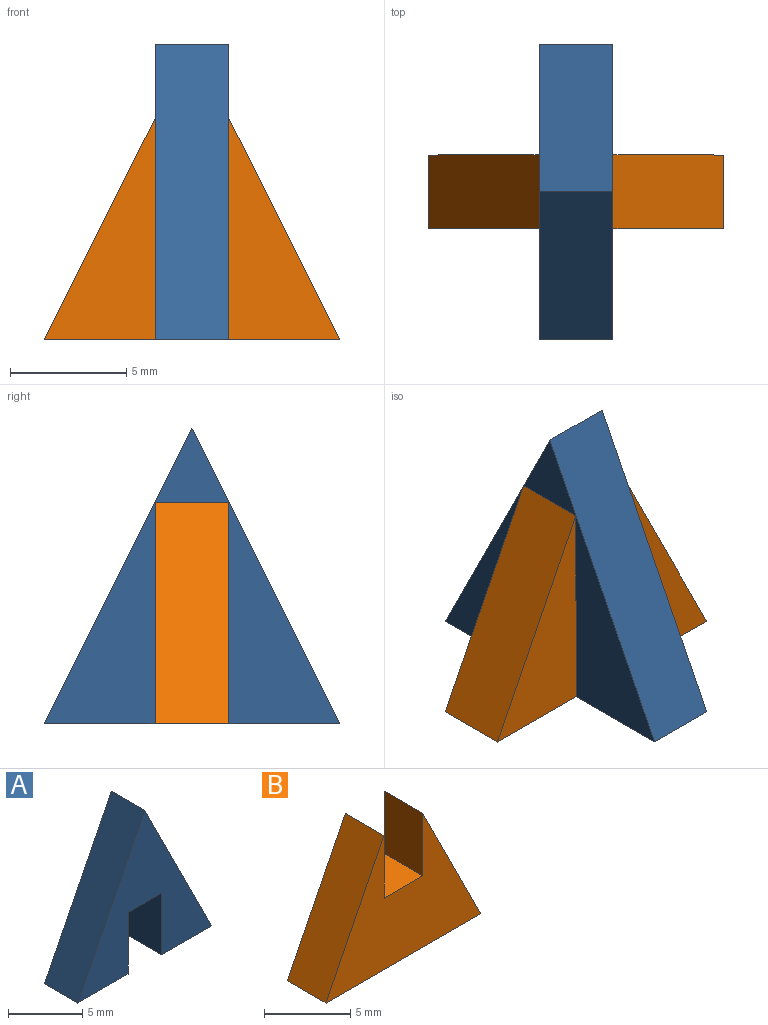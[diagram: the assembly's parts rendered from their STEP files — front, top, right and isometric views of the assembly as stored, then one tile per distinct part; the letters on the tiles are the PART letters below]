
ASSEMBLY  parts=2 mates=1
PART A: 9 faces, bbox 12.7x3.2x12.7 mm
  f0: plane 5.08x3.18mm, normal (-1,0,0), area 16.1mm2, adj f1,f6,f7,f8
  f1: plane 4.76x3.18mm, normal (0,0,-1), area 15.1mm2, adj f0,f2,f7,f8
  f2: plane 12.7x6.35mm, normal (0.89,0,0.45), area 45.1mm2, adj f1,f3,f7,f8
  f3: plane 12.7x6.35mm, normal (-0.89,0,0.45), area 45.1mm2, adj f2,f4,f7,f8
  f4: plane 4.76x3.18mm, normal (0,0,-1), area 15.1mm2, adj f3,f5,f7,f8
  f5: plane 5.08x3.18mm, normal (1,0,0), area 16.1mm2, adj f4,f6,f7,f8
  f6: plane 3.18x3.18mm, normal (0,0,-1), area 10.1mm2, adj f0,f5,f7,f8
  f7: plane 12.7x12.7mm, normal (0,-1,0), area 64.5mm2, adj f0,f1,f2,f3,f4,f5,f6
  f8: plane 12.7x12.7mm, normal (0,1,0), area 64.5mm2, adj f0,f1,f2,f3,f4,f5,f6
PART B: 8 faces, bbox 12.7x3.2x9.5 mm
  f0: plane 12.7x3.18mm, normal (0,0,-1), area 40.3mm2, adj f1,f5,f6,f7
  f1: plane 9.53x4.76mm, normal (0.89,0,0.45), area 33.8mm2, adj f0,f2,f6,f7
  f2: plane 4.45x3.18mm, normal (-1,0,0), area 14.1mm2, adj f1,f3,f6,f7
  f3: plane 3.18x3.18mm, normal (0,0,1), area 10.1mm2, adj f2,f4,f6,f7
  f4: plane 4.45x3.18mm, normal (1,0,0), area 14.1mm2, adj f3,f5,f6,f7
  f5: plane 9.53x4.76mm, normal (-0.89,0,0.45), area 33.8mm2, adj f0,f4,f6,f7
  f6: plane 12.7x9.53mm, normal (0,-1,0), area 61.5mm2, adj f0,f1,f2,f3,f4,f5
  f7: plane 12.7x9.53mm, normal (0,1,0), area 61.5mm2, adj f0,f1,f2,f3,f4,f5
PLACE A rot(axis=(0,0,1),90deg) t=(3.16,4,0.46)mm
PLACE B t=(8.95,7.17,26.5)mm
MATE fastened A.f6 <-> B.f3  axis (0,0,-1) through (4.74,5.58,5.54)mm
